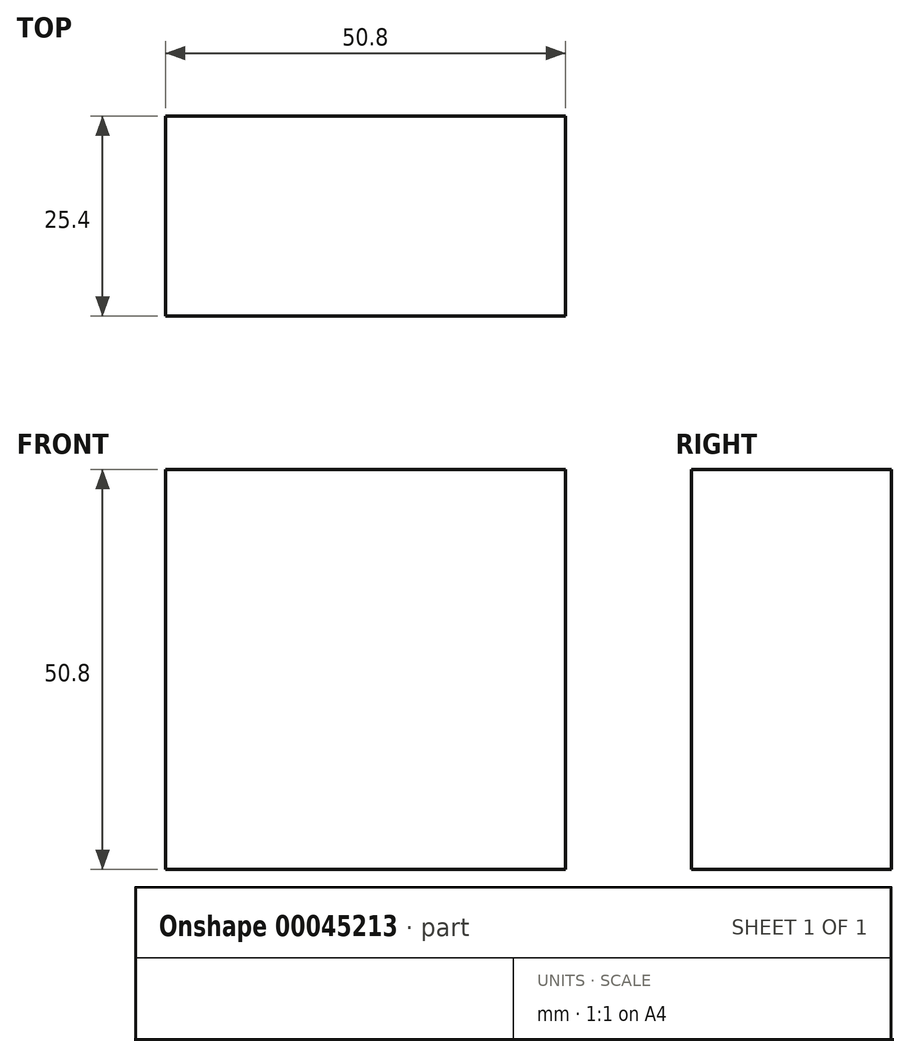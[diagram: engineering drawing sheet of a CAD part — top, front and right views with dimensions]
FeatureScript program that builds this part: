
annotation { "Feature Type Name" : "Feature", "Feature Type Description" : "" }
export const myFeature = defineFeature(function(context is Context, id is Id, definition is map)
    precondition{}
    {
        {
            var Q0;
            Q0=qCreatedBy(makeId("Front.planeOp"),FACE);
            var sketch = newSketch(context, id + "F0", { "sketchPlane" : qUnion([Q0])});
            skLineSegment(sketch, "E0.rect.bottom", {"start": v(25.4, -25.4) * mm, "end": v(-25.4, -25.4) * mm});
            skLineSegment(sketch, "E0.rect.top", {"start": v(25.4, 25.4) * mm, "end": v(-25.4, 25.4) * mm});
            skLineSegment(sketch, "E0.rect.left", {"start": v(25.4, -25.4) * mm, "end": v(25.4, 25.4) * mm});
            skLineSegment(sketch, "E0.rect.right", {"start": v(-25.4, -25.4) * mm, "end": v(-25.4, 25.4) * mm});
            skPoint(sketch, "E0.rect.middle", {"position": v(0, 0) * mm});
            skSolve(sketch);
        }
        {
            var Q0;
            Q0=qSketchRegion(id+"F0",true);
            extrude(context, id + "F1", {"entities" : qUnion([Q0]), "depth" : 25.4 * mm});
        }
    });
